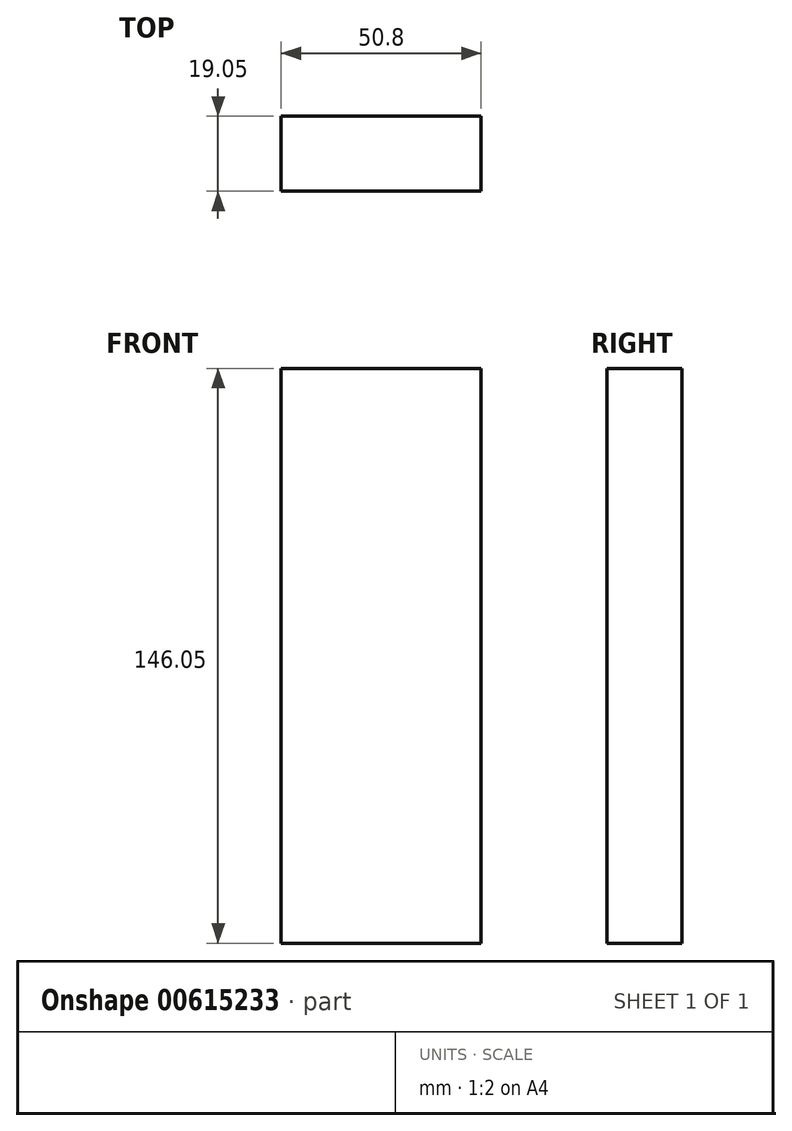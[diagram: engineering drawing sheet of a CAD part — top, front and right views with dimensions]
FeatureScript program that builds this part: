
annotation { "Feature Type Name" : "Feature", "Feature Type Description" : "" }
export const myFeature = defineFeature(function(context is Context, id is Id, definition is map)
    precondition{}
    {
        {
            var Q0;
            Q0=qCreatedBy(makeId("Top.planeOp"),FACE);
            var sketch = newSketch(context, id + "F0", { "sketchPlane" : qUnion([Q0])});
            skLineSegment(sketch, "E0.bottom", {"start": v(0, 0) * mm, "end": v(50.8, 0) * mm});
            skLineSegment(sketch, "E0.top", {"start": v(0, 19.05) * mm, "end": v(50.8, 19.05) * mm});
            skLineSegment(sketch, "E0.left", {"start": v(0, 0) * mm, "end": v(0, 19.05) * mm});
            skLineSegment(sketch, "E0.right", {"start": v(50.8, 0) * mm, "end": v(50.8, 19.05) * mm});
            skSolve(sketch);
        }
        {
            var Q0;
            Q0=makeQuery(id+"F0.imprint","IMPRINT",FACE,{"disambiguationData":[TD([[makeQuery(id+"F0.imprint","IMPRINT",EDGE,{"derivedFrom":sQuery(id+"F0.wireOp",EDGE,"E0.bottom")}),1.0]])]});
            extrude(context, id + "F1", {"entities" : qUnion([Q0]), "depth" : 146.05 * mm, "offsetDistance" : 25.4 * mm});
        }
    });
